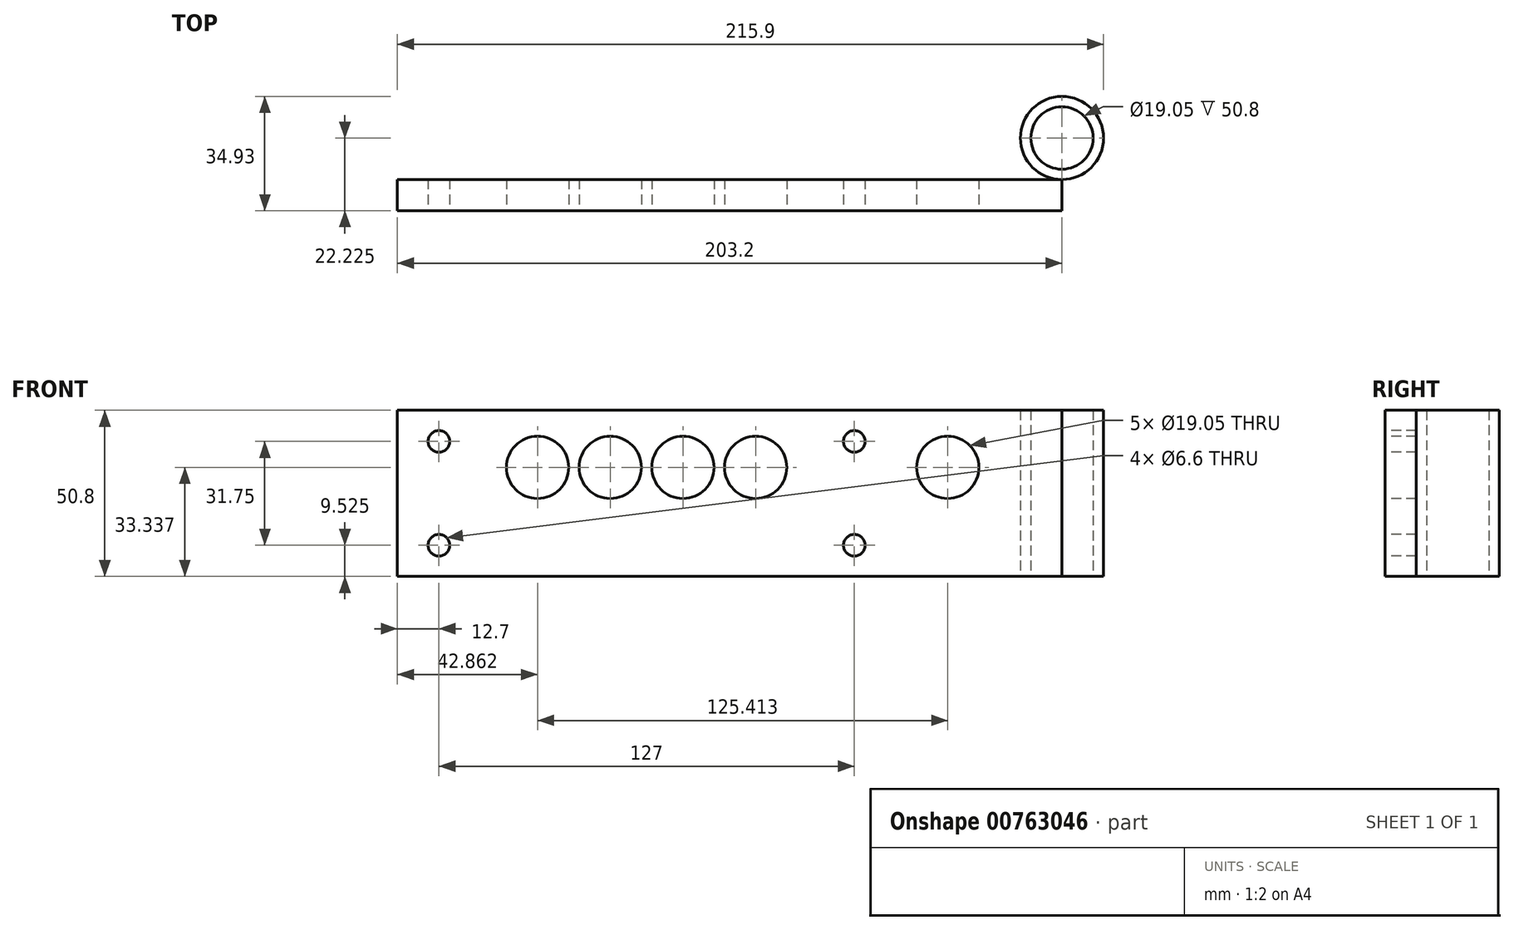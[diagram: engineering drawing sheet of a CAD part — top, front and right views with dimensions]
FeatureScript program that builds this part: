
annotation { "Feature Type Name" : "Feature", "Feature Type Description" : "" }
export const myFeature = defineFeature(function(context is Context, id is Id, definition is map)
    precondition{}
    {
        {
            var Q0;
            Q0=qCreatedBy(makeId("Front.planeOp"),FACE);
            var sketch = newSketch(context, id + "F0", { "sketchPlane" : qUnion([Q0])});
            skLineSegment(sketch, "E0.bottom", {"start": v(0, 0) * mm, "end": v(203.2, 0) * mm});
            skLineSegment(sketch, "E0.top", {"start": v(0, 50.8) * mm, "end": v(203.2, 50.8) * mm});
            skLineSegment(sketch, "E0.left", {"start": v(0, 0) * mm, "end": v(0, 50.8) * mm});
            skLineSegment(sketch, "E0.right", {"start": v(203.2, 0) * mm, "end": v(203.2, 50.8) * mm});
            skCircle(sketch, "E1", {"center": v(12.7, 9.53) * mm, "radius": 3.3 * mm});
            skCircle(sketch, "E2.0.1.0", {"center": v(12.7, 41.27) * mm, "radius": 3.3 * mm});
            skCircle(sketch, "E2.1.0.0", {"center": v(139.7, 9.53) * mm, "radius": 3.3 * mm});
            skCircle(sketch, "E2.1.1.0", {"center": v(139.7, 41.27) * mm, "radius": 3.3 * mm});
            skLineSegment(sketch, "E2.direction1", {"start": v(12.7, 9.53) * mm, "end": v(139.7, 9.53) * mm, "construction": true});
            skLineSegment(sketch, "E2.direction2", {"start": v(12.7, 9.52) * mm, "end": v(12.7, 41.27) * mm, "construction": true});
            skCircle(sketch, "E3", {"center": v(42.86, 33.34) * mm, "radius": 9.53 * mm});
            skCircle(sketch, "E4.1.0.0", {"center": v(65.09, 33.34) * mm, "radius": 9.53 * mm});
            skCircle(sketch, "E4.2.0.0", {"center": v(87.31, 33.34) * mm, "radius": 9.53 * mm});
            skCircle(sketch, "E4.3.0.0", {"center": v(109.54, 33.34) * mm, "radius": 9.53 * mm});
            skLineSegment(sketch, "E4.direction1", {"start": v(42.86, 33.34) * mm, "end": v(65.09, 33.34) * mm, "construction": true});
            skCircle(sketch, "E5", {"center": v(168.28, 33.34) * mm, "radius": 9.53 * mm});
            skSolve(sketch);
        }
        {
            var Q0;
            Q0 = qSketchRegion(id + "F0", true);
            extrude(context, id + "F1", {"entities" : qUnion([Q0]), "oppositeDirection" : true, "depth" : 9.52 * mm, "offsetDistance" : 25.4 * mm});
        }
        {
            var Q0;
            Q0=qCreatedBy(makeId("Top.planeOp"),FACE);
            var sketch = newSketch(context, id + "F2", { "sketchPlane" : qUnion([Q0])});
            skCircle(sketch, "E6", {"center": v(203.2, 22.23) * mm, "radius": 12.7 * mm});
            skCircle(sketch, "E7", {"center": v(203.2, 22.23) * mm, "radius": 9.53 * mm});
            skSolve(sketch);
        }
        {
            var Q0;
            Q0 = qSketchRegion(id + "F2", true);
            extrude(context, id + "F3", {"entities" : qUnion([Q0]), "depth" : 50.8 * mm, "offsetDistance" : 25.4 * mm});
        }
    });
